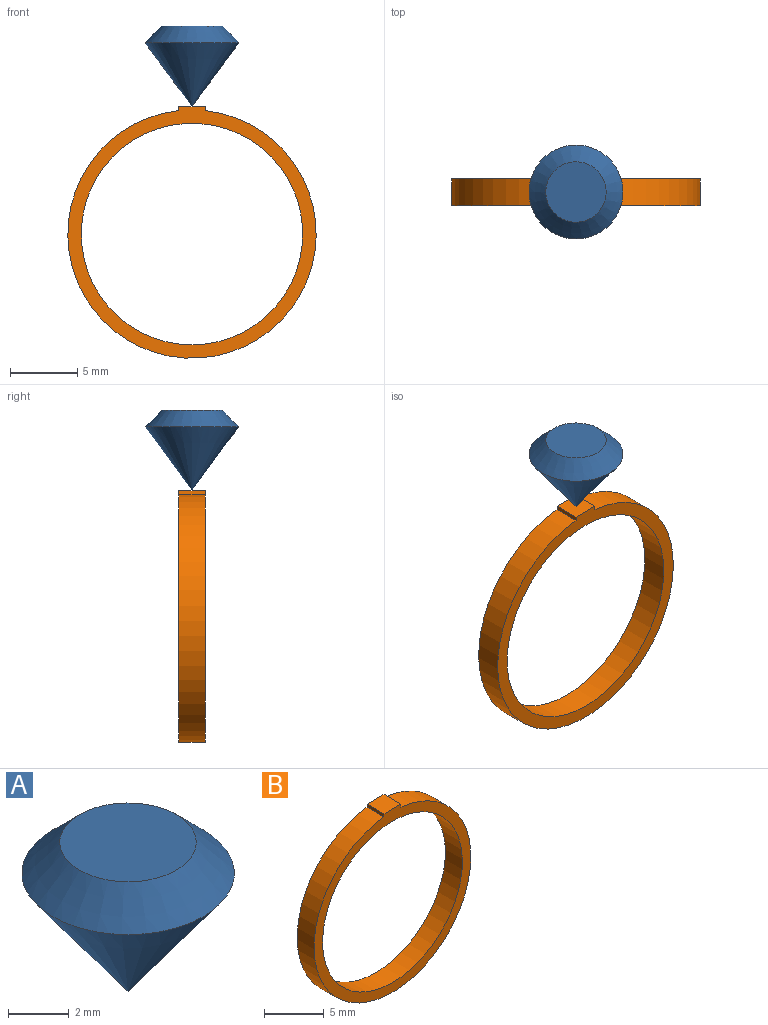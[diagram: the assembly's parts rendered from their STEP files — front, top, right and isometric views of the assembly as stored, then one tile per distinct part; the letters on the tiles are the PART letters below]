
ASSEMBLY  parts=2 mates=1
PART A: 3 faces, bbox 7x7x6 mm
  f0: cone r=0mm half-angle=36.4deg, axis (0,0,1), area 64.9mm2, adj f1
  f1: cone r=2.25mm half-angle=45deg, axis (0,0,-1), area 31.9mm2, adj f0,f2
  f2: plane 4.5x4.5mm, normal (0,0,1), area 15.9mm2, adj f1
PART B: 7 faces, bbox 18.5x2x18.8 mm
  f0: cylinder r=8.25mm len=16.5mm, axis (0,1,0), area 103.7mm2, adj f2,f3
  f1: cylinder r=9.25mm len=18.5mm, axis (0,1,0), area 112.2mm2, adj f2,f3,f4,f5
  f2: plane 18.75x18.5mm, normal (0,-1,0), area 55.5mm2, adj f0,f1,f4,f5,f6
  f3: plane 18.75x18.5mm, normal (0,1,0), area 55.5mm2, adj f0,f1,f4,f5,f6
  f4: plane 2x0.3mm, normal (-1,0,0), area 0.6mm2, adj f1,f2,f3,f6
  f5: plane 2x0.3mm, normal (1,0,0), area 0.6mm2, adj f1,f2,f3,f6
  f6: plane 2x2mm, normal (0,0,1), area 4mm2, adj f2,f3,f4,f5
PLACE A t=(-15.44,-18.73,-8.77)mm
PLACE B t=(-15.44,-17.73,-18.27)mm
MATE fastened A.f0 <-> B.f6  axis (0,0,1) through (-15.44,-18.73,-8.77)mm
